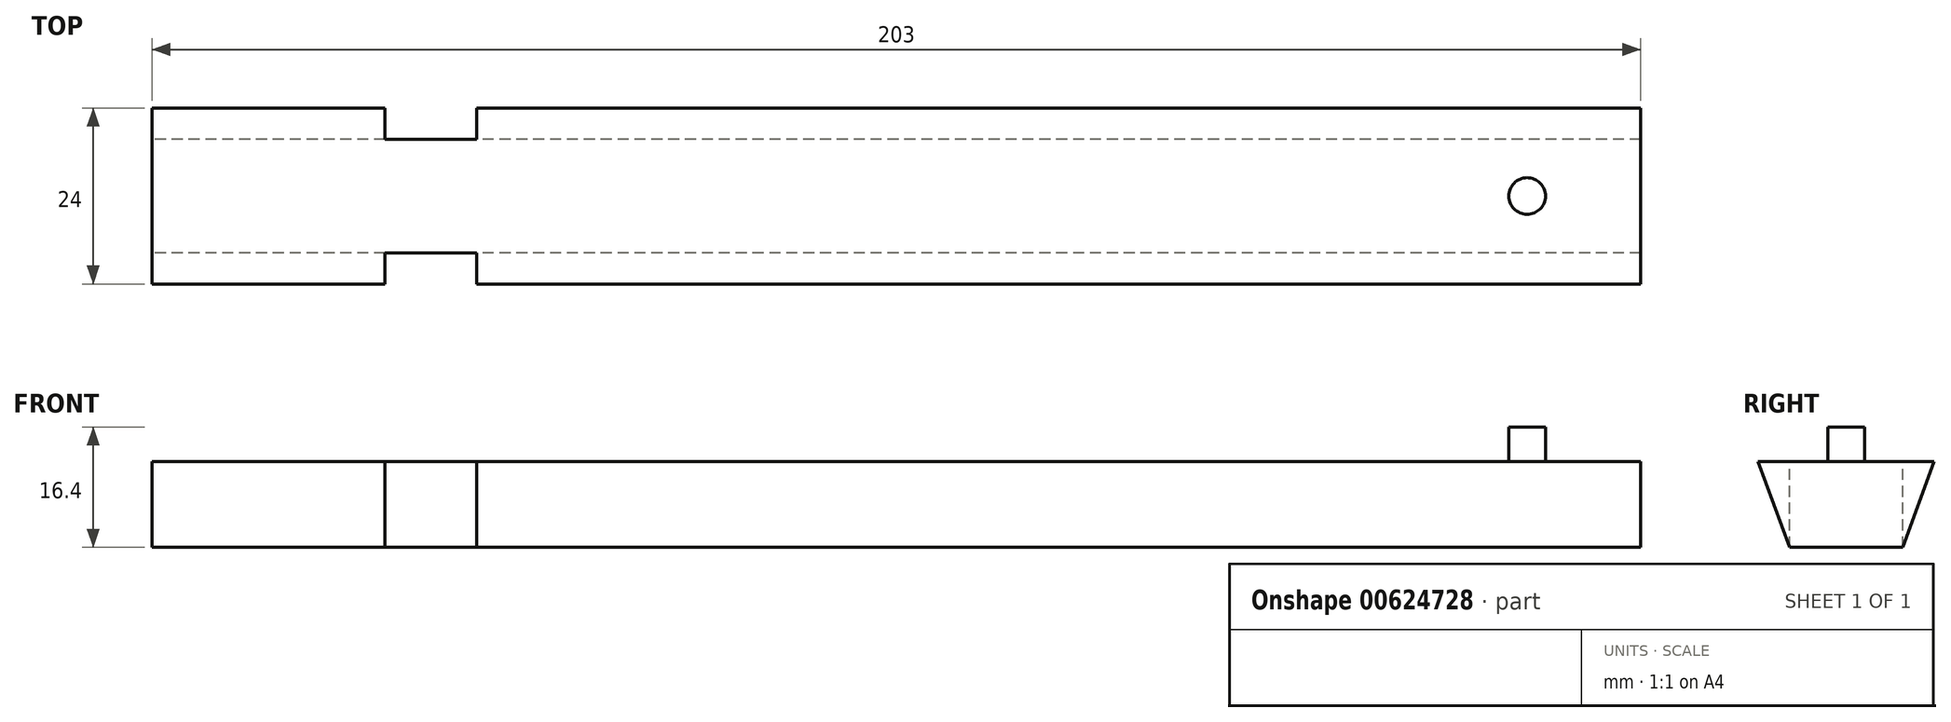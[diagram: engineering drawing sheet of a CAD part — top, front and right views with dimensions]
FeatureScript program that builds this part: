
annotation { "Feature Type Name" : "Feature", "Feature Type Description" : "" }
export const myFeature = defineFeature(function(context is Context, id is Id, definition is map)
    precondition{}
    {
        {
            var Q0;
            Q0=qCreatedBy(makeId("Right.planeOp"),FACE);
            var sketch = newSketch(context, id + "F0", { "sketchPlane" : qUnion([Q0])});
            skLineSegment(sketch, "E0", {"start": v(-7.74, 0) * mm, "end": v(-12, 11.7) * mm});
            skLineSegment(sketch, "E1", {"start": v(-12, 11.7) * mm, "end": v(0, 11.7) * mm});
            skLineSegment(sketch, "E2", {"start": v(0, 11.7) * mm, "end": v(0, 0) * mm});
            skLineSegment(sketch, "E3", {"start": v(0, 0) * mm, "end": v(-7.74, 0) * mm});
            skLineSegment(sketch, "E4.MirrorCS", {"start": v(12, 11.7) * mm, "end": v(0, 11.7) * mm});
            skLineSegment(sketch, "E5.MirrorCS", {"start": v(7.74, 0) * mm, "end": v(12, 11.7) * mm});
            skLineSegment(sketch, "E6.MirrorCS", {"start": v(0, 0) * mm, "end": v(7.74, 0) * mm});
            skSolve(sketch);
        }
        {
            var Q0;
            Q0 = qSketchRegion(id + "F0", true);
            extrude(context, id + "F1", {"entities" : qUnion([Q0]), "depth" : 203 * mm, "offsetDistance" : 25 * mm});
        }
        {
            var Q0;
            Q0=makeQuery(id+"F1.opExtrude","SWEPT_FACE",FACE,{"disambiguationData":[OSD([sQuery(id+"F0.wireOp",EDGE,"E1"),sQuery(id+"F0.wireOp",EDGE,"E4.MirrorCS")])]});
            var sketch = newSketch(context, id + "F2", { "sketchPlane" : qUnion([Q0])});
            skLineSegment(sketch, "E7", {"start": v(-8.72, 0) * mm, "end": v(111.18, 0) * mm, "construction": true});
            skCircle(sketch, "E8", {"center": v(187.5, 0) * mm, "radius": 2.5 * mm});
            skSolve(sketch);
        }
        {
            var Q0;
            Q0=makeQuery(id+"F2.imprint","IMPRINT",FACE,{"disambiguationData":[TD([[makeQuery(id+"F2.imprint","IMPRINT",EDGE,{"derivedFrom":sQuery(id+"F2.wireOp",EDGE,"E8")}),1.0]])]});
            extrude(context, id + "F3", {"entities" : qUnion([Q0]), "operationType" : NewBodyOperationType.REMOVE, "oppositeDirection" : true, "depth" : 10 * mm, "offsetDistance" : 25 * mm});
        }
        {
            var Q0;
            Q0=makeQuery(id+"F1.opExtrude","SWEPT_FACE",FACE,{"disambiguationData":[OSD([sQuery(id+"F0.wireOp",EDGE,"E1"),sQuery(id+"F0.wireOp",EDGE,"E4.MirrorCS")])]});
            var sketch = newSketch(context, id + "F4", { "sketchPlane" : qUnion([Q0])});
            skLineSegment(sketch, "E9.0", {"start": v(203, 7.74) * mm, "end": v(0, 7.74) * mm});
            skLineSegment(sketch, "E10.0", {"start": v(203, -7.74) * mm, "end": v(0, -7.74) * mm});
            skLineSegment(sketch, "E11", {"start": v(31.8, 12) * mm, "end": v(31.8, 7.74) * mm});
            skLineSegment(sketch, "E12", {"start": v(31.8, 7.74) * mm, "end": v(44.3, 7.74) * mm});
            skLineSegment(sketch, "E13", {"start": v(44.3, 7.74) * mm, "end": v(44.3, 12) * mm});
            skLineSegment(sketch, "E14", {"start": v(31.8, 12) * mm, "end": v(44.3, 12) * mm});
            skLineSegment(sketch, "E15.MirrorCS", {"start": v(31.8, -12) * mm, "end": v(31.8, -7.74) * mm});
            skLineSegment(sketch, "E16.MirrorCS", {"start": v(31.8, -12) * mm, "end": v(44.3, -12) * mm});
            skLineSegment(sketch, "E17.MirrorCS", {"start": v(44.3, -7.74) * mm, "end": v(44.3, -12) * mm});
            skSolve(sketch);
        }
        {
            var Q0;
            Q0 = qSketchRegion(id + "F4", true);
            extrude(context, id + "F5", {"entities" : qUnion([Q0]), "operationType" : NewBodyOperationType.REMOVE, "endBound" : BoundingType.THROUGH_ALL, "oppositeDirection" : true, "depth" : 25 * mm, "offsetDistance" : 25 * mm});
        }
        {
            var Q0;
            Q0=makeQuery(id+"F3.boolean.opBoolean","COPY",FACE,{"derivedFrom":makeQuery(id+"F3.opExtrude","CAP_FACE",FACE,{"disambiguationData":[OSD([sQuery(id+"F2.wireOp",EDGE,"E8")])],"isStart":false})});
            extrude(context, id + "F6", {"entities" : qUnion([Q0]), "operationType" : NewBodyOperationType.ADD, "depth" : 14.7 * mm, "offsetDistance" : 25 * mm});
        }
    });
